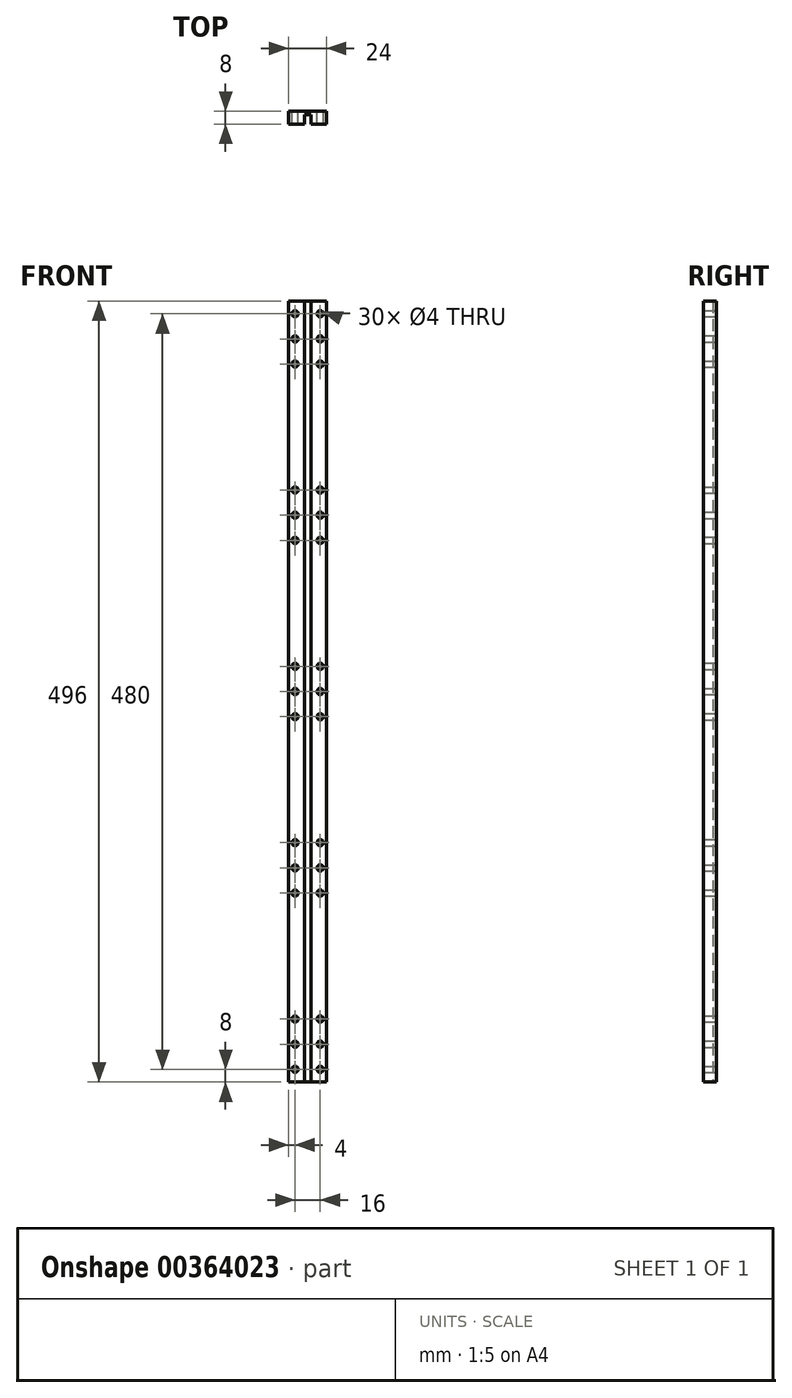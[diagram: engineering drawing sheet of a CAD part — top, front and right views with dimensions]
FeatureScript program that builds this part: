
annotation { "Feature Type Name" : "Feature", "Feature Type Description" : "" }
export const myFeature = defineFeature(function(context is Context, id is Id, definition is map)
    precondition{}
    {
        {
            var Q0;
            Q0=qCreatedBy(makeId("Top.planeOp"),FACE);
            var sketch = newSketch(context, id + "F0", { "sketchPlane" : qUnion([Q0])});
            skLineSegment(sketch, "E0.top", {"start": v(12, 4) * mm, "end": v(-12, 4) * mm});
            skLineSegment(sketch, "E0.left", {"start": v(12, -4) * mm, "end": v(12, 4) * mm});
            skLineSegment(sketch, "E0.right", {"start": v(-12, -4) * mm, "end": v(-12, 4) * mm});
            skPoint(sketch, "E0.middle", {"position": v(0, 0) * mm});
            skLineSegment(sketch, "E1", {"start": v(-12, -4) * mm, "end": v(-2, -4) * mm});
            skLineSegment(sketch, "E2", {"start": v(-2, -4) * mm, "end": v(-2, 2) * mm});
            skLineSegment(sketch, "E3", {"start": v(-2, 2) * mm, "end": v(2, 2) * mm});
            skLineSegment(sketch, "E4", {"start": v(2, 2) * mm, "end": v(2, -4) * mm});
            skLineSegment(sketch, "E5", {"start": v(2, -4) * mm, "end": v(12, -4) * mm});
            skSolve(sketch);
        }
        {
            var Q0;
            Q0 = qSketchRegion(id + "F0", true);
            extrude(context, id + "F1", {"entities" : qUnion([Q0]), "depth" : 496 * mm});
        }
        {
            var Q0;
            Q0=makeQuery(id+"F1.opExtrude","SWEPT_FACE",FACE,{"disambiguationData":[OSD([sQuery(id+"F0.wireOp",EDGE,"E0.top")])]});
            var sketch = newSketch(context, id + "F2", { "sketchPlane" : qUnion([Q0])});
            skLineSegment(sketch, "E6", {"start": v(-8, 0) * mm, "end": v(-8, 8) * mm, "construction": true});
            skLineSegment(sketch, "E7", {"start": v(-8, 8) * mm, "end": v(-8, 24) * mm, "construction": true});
            skLineSegment(sketch, "E8", {"start": v(-8, 24) * mm, "end": v(-8, 40) * mm, "construction": true});
            skCircle(sketch, "E9", {"center": v(-8, 40) * mm, "radius": 2 * mm});
            skCircle(sketch, "E10", {"center": v(-8, 24) * mm, "radius": 2 * mm});
            skCircle(sketch, "E11", {"center": v(-8, 8) * mm, "radius": 2 * mm});
            skCircle(sketch, "E12.0.1.0", {"center": v(-8, 120) * mm, "radius": 2 * mm});
            skCircle(sketch, "E12.0.1.1", {"center": v(-8, 136) * mm, "radius": 2 * mm});
            skCircle(sketch, "E12.0.1.2", {"center": v(-8, 152) * mm, "radius": 2 * mm});
            skCircle(sketch, "E12.0.2.0", {"center": v(-8, 232) * mm, "radius": 2 * mm});
            skCircle(sketch, "E12.0.2.1", {"center": v(-8, 248) * mm, "radius": 2 * mm});
            skCircle(sketch, "E12.0.2.2", {"center": v(-8, 264) * mm, "radius": 2 * mm});
            skCircle(sketch, "E12.0.3.0", {"center": v(-8, 344) * mm, "radius": 2 * mm});
            skCircle(sketch, "E12.0.3.1", {"center": v(-8, 360) * mm, "radius": 2 * mm});
            skCircle(sketch, "E12.0.3.2", {"center": v(-8, 376) * mm, "radius": 2 * mm});
            skCircle(sketch, "E12.0.4.0", {"center": v(-8, 456) * mm, "radius": 2 * mm});
            skCircle(sketch, "E12.0.4.1", {"center": v(-8, 472) * mm, "radius": 2 * mm});
            skCircle(sketch, "E12.0.4.2", {"center": v(-8, 488) * mm, "radius": 2 * mm});
            skLineSegment(sketch, "E12.direction1", {"start": v(-8, 8) * mm, "end": v(17, 8) * mm, "construction": true});
            skLineSegment(sketch, "E12.direction2", {"start": v(-8, 8) * mm, "end": v(-8, 120) * mm, "construction": true});
            skCircle(sketch, "E13.MirrorC", {"center": v(8, 8) * mm, "radius": 2 * mm});
            skCircle(sketch, "E14.MirrorC", {"center": v(8, 24) * mm, "radius": 2 * mm});
            skCircle(sketch, "E15.MirrorC", {"center": v(8, 40) * mm, "radius": 2 * mm});
            skCircle(sketch, "E16.MirrorC", {"center": v(8, 120) * mm, "radius": 2 * mm});
            skCircle(sketch, "E17.MirrorC", {"center": v(8, 136) * mm, "radius": 2 * mm});
            skCircle(sketch, "E18.MirrorC", {"center": v(8, 152) * mm, "radius": 2 * mm});
            skCircle(sketch, "E19.MirrorC", {"center": v(8, 232) * mm, "radius": 2 * mm});
            skCircle(sketch, "E20.MirrorC", {"center": v(8, 264) * mm, "radius": 2 * mm});
            skCircle(sketch, "E21.MirrorC", {"center": v(8, 248) * mm, "radius": 2 * mm});
            skCircle(sketch, "E22.MirrorC", {"center": v(8, 344) * mm, "radius": 2 * mm});
            skCircle(sketch, "E23.MirrorC", {"center": v(8, 360) * mm, "radius": 2 * mm});
            skCircle(sketch, "E24.MirrorC", {"center": v(8, 376) * mm, "radius": 2 * mm});
            skCircle(sketch, "E25.MirrorC", {"center": v(8, 456) * mm, "radius": 2 * mm});
            skCircle(sketch, "E26.MirrorC", {"center": v(8, 472) * mm, "radius": 2 * mm});
            skCircle(sketch, "E27.MirrorC", {"center": v(8, 488) * mm, "radius": 2 * mm});
            skSolve(sketch);
        }
        {
            var Q0;
            Q0 = qSketchRegion(id + "F2", true);
            extrude(context, id + "F3", {"entities" : qUnion([Q0]), "operationType" : NewBodyOperationType.REMOVE, "oppositeDirection" : true, "depth" : 25 * mm});
        }
    });
